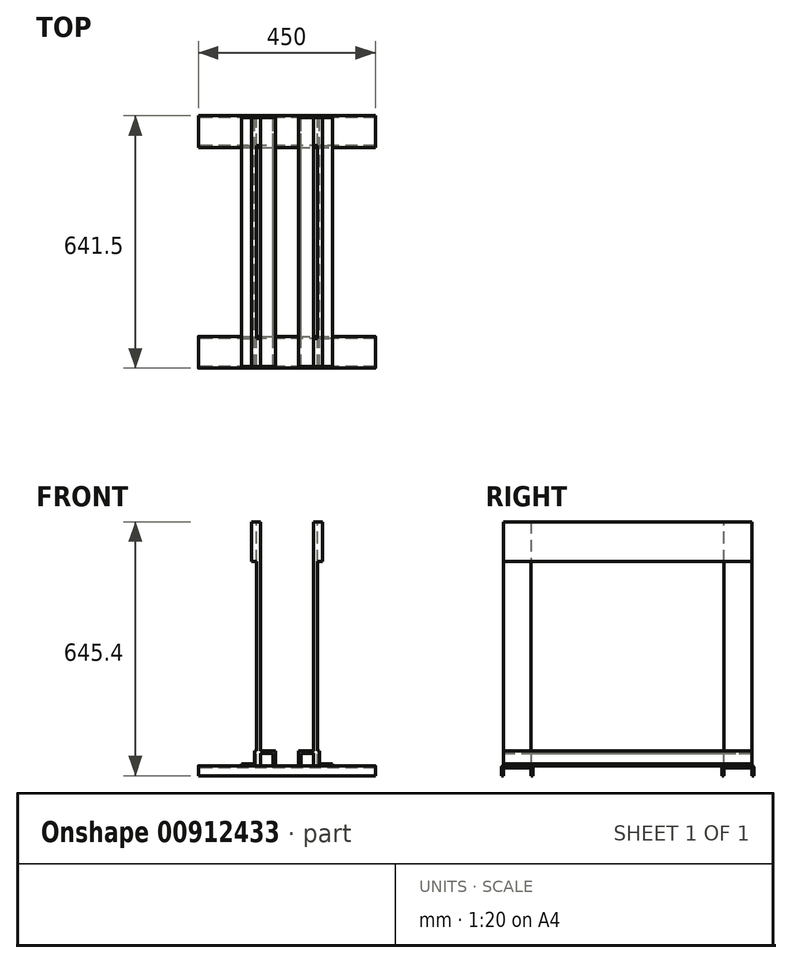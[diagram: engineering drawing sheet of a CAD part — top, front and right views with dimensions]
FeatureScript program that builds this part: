
annotation { "Feature Type Name" : "Feature", "Feature Type Description" : "" }
export const myFeature = defineFeature(function(context is Context, id is Id, definition is map)
    precondition{}
    {
        {
            var Q0;
            Q0=qCreatedBy(makeId("Front.planeOp"),FACE);
            var sketch = newSketch(context, id + "F0", { "sketchPlane" : qUnion([Q0])});
            skLineSegment(sketch, "E0.bottom", {"start": v(0, 0) * mm, "end": v(-10.45, 0) * mm});
            skLineSegment(sketch, "E0.top", {"start": v(0, 620) * mm, "end": v(-10.45, 620) * mm});
            skLineSegment(sketch, "E0.left", {"start": v(0, 0) * mm, "end": v(0, 620) * mm});
            skLineSegment(sketch, "E0.right", {"start": v(-10.45, 0) * mm, "end": v(-10.45, 620) * mm});
            skLineSegment(sketch, "E1", {"start": v(0, 38.1) * mm, "end": v(38.1, 38.1) * mm});
            skLineSegment(sketch, "E2", {"start": v(38.1, 38.1) * mm, "end": v(38.1, 0) * mm});
            skLineSegment(sketch, "E3", {"start": v(38.1, 0) * mm, "end": v(31.75, 0) * mm});
            skLineSegment(sketch, "E4", {"start": v(31.75, 0) * mm, "end": v(31.75, 31.75) * mm});
            skLineSegment(sketch, "E5", {"start": v(31.75, 31.75) * mm, "end": v(0, 31.75) * mm});
            skSolve(sketch);
        }
        {
            var Q0;
            {var subQ0=sQuery(id+"F0.wireOp",EDGE,"E1");Q0=makeQuery(id+"F0.imprint","IMPRINT",FACE,{"disambiguationData":[TD([[makeQuery(id+"F0.imprint","IMPRINT",EDGE,{"derivedFrom":subQ0}),-1.0]])]});}
            extrude(context, id + "F1", {"entities" : qUnion([Q0]), "depth" : 631.5 * mm, "offsetDistance" : 25 * mm});
        }
        {
            var Q0;
            {var subQ3=sQuery(id+"F0.wireOp",EDGE,"E0.bottom");Q0=makeQuery(id+"F0.imprint","IMPRINT",FACE,{"disambiguationData":[TD([[makeQuery(id+"F0.imprint","IMPRINT",EDGE,{"derivedFrom":subQ3}),-1.0]])]});}
            extrude(context, id + "F2", {"entities" : qUnion([Q0]), "operationType" : NewBodyOperationType.ADD, "depth" : 70.75 * mm, "offsetDistance" : 25 * mm});
        }
        {
            var Q0;
            Q0=qCreatedBy(makeId("Top.planeOp"),FACE);
            var sketch = newSketch(context, id + "F3", { "sketchPlane" : qUnion([Q0])});
            skLineSegment(sketch, "E6.bottom", {"start": v(0, -631.5) * mm, "end": v(-10.45, -631.5) * mm});
            skLineSegment(sketch, "E6.top", {"start": v(0, -560.75) * mm, "end": v(-10.45, -560.75) * mm});
            skLineSegment(sketch, "E6.left", {"start": v(0, -631.5) * mm, "end": v(0, -560.75) * mm});
            skLineSegment(sketch, "E6.right", {"start": v(-10.45, -631.5) * mm, "end": v(-10.45, -560.75) * mm});
            skSolve(sketch);
        }
        {
            var Q0;
            Q0 = qSketchRegion(id + "F3", true);
            extrude(context, id + "F4", {"entities" : qUnion([Q0]), "operationType" : NewBodyOperationType.ADD, "depth" : 620 * mm, "offsetDistance" : 25 * mm});
        }
        {
            var Q0;
            Q0=qCreatedBy(makeId("Top.planeOp"),FACE);
            var sketch = newSketch(context, id + "F5", { "sketchPlane" : qUnion([Q0])});
            skLineSegment(sketch, "E7.bottom", {"start": v(-157.8, 5) * mm, "end": v(292.2, 5) * mm});
            skLineSegment(sketch, "E7.top", {"start": v(-157.8, -75.75) * mm, "end": v(292.2, -75.75) * mm});
            skLineSegment(sketch, "E7.left", {"start": v(-157.8, 5) * mm, "end": v(-157.8, -75.75) * mm});
            skLineSegment(sketch, "E7.right", {"start": v(292.2, 5) * mm, "end": v(292.2, -75.75) * mm});
            skLineSegment(sketch, "E8.bottom", {"start": v(-157.8, -636.5) * mm, "end": v(292.2, -636.5) * mm});
            skLineSegment(sketch, "E8.top", {"start": v(-157.8, -555.75) * mm, "end": v(292.2, -555.75) * mm});
            skLineSegment(sketch, "E8.left", {"start": v(-157.8, -636.5) * mm, "end": v(-157.8, -555.75) * mm});
            skLineSegment(sketch, "E8.right", {"start": v(292.2, -636.5) * mm, "end": v(292.2, -555.75) * mm});
            skSolve(sketch);
        }
        {
            var Q0;
            Q0 = qSketchRegion(id + "F5", true);
            extrude(context, id + "F6", {"entities" : qUnion([Q0]), "operationType" : NewBodyOperationType.ADD, "oppositeDirection" : true, "depth" : 25.4 * mm, "offsetDistance" : 25 * mm});
        }
        {
            var Q0;
            Q0=makeQuery(id+"F6.opExtrude","CAP_EDGE",EDGE,{"disambiguationData":[OSD([sQuery(id+"F5.wireOp",EDGE,"E8.bottom")])],"isStart":true});
            var Q1;
            {var subQ0=sQuery(id+"F5.wireOp",EDGE,"E8.top");var subQ1=makeQuery(id+"F6.opExtrude","SWEPT_FACE",FACE,{"disambiguationData":[OSD([subQ0])]});var subQ2=sQuery(id+"F5.wireOp",EDGE,"E8.right");var subQ3=makeQuery(id+"F6.opExtrude","CAP_FACE",FACE,{"disambiguationData":[OSD([sQuery(id+"F5.wireOp",EDGE,"E8.bottom"),subQ0,sQuery(id+"F5.wireOp",EDGE,"E8.left"),subQ2])],"isStart":true});Q1=makeQuery(id+"F6.boolean.opBoolean","SPLIT",EDGE,{"disambiguationData":[topologyDisambiguationEdgeConnected([subQ3,subQ1]),TD([makeQuery(id+"F1.opExtrude","SWEPT_FACE",FACE,{"disambiguationData":[OSD([sQuery(id+"F0.wireOp",EDGE,"E2")])]})])],"derivedFrom":makeQuery(id+"F6.opExtrude","CAP_EDGE",EDGE,{"disambiguationData":[OSD([subQ0])],"isStart":true})});}
            var Q2;
            {var subQ0=sQuery(id+"F5.wireOp",EDGE,"E8.top");var subQ1=makeQuery(id+"F6.opExtrude","SWEPT_FACE",FACE,{"disambiguationData":[OSD([subQ0])]});var subQ2=sQuery(id+"F5.wireOp",EDGE,"E8.left");var subQ3=makeQuery(id+"F6.opExtrude","CAP_FACE",FACE,{"disambiguationData":[OSD([sQuery(id+"F5.wireOp",EDGE,"E8.bottom"),subQ0,subQ2,sQuery(id+"F5.wireOp",EDGE,"E8.right")])],"isStart":true});Q2=makeQuery(id+"F6.boolean.opBoolean","SPLIT",EDGE,{"disambiguationData":[topologyDisambiguationEdgeConnected([subQ3,subQ1]),TD([makeQuery(id+"F1.opExtrude","SWEPT_FACE",FACE,{"disambiguationData":[OSD([sQuery(id+"F0.wireOp",EDGE,"E4")])]})])],"derivedFrom":makeQuery(id+"F6.opExtrude","CAP_EDGE",EDGE,{"disambiguationData":[OSD([subQ0])],"isStart":true})});}
            var Q3;
            {var subQ0=sQuery(id+"F5.wireOp",EDGE,"E7.top");var subQ1=makeQuery(id+"F6.opExtrude","SWEPT_FACE",FACE,{"disambiguationData":[OSD([subQ0])]});var subQ2=sQuery(id+"F5.wireOp",EDGE,"E7.right");var subQ3=makeQuery(id+"F6.opExtrude","CAP_FACE",FACE,{"disambiguationData":[OSD([sQuery(id+"F5.wireOp",EDGE,"E7.bottom"),subQ0,sQuery(id+"F5.wireOp",EDGE,"E7.left"),subQ2])],"isStart":true});Q3=makeQuery(id+"F6.boolean.opBoolean","SPLIT",EDGE,{"disambiguationData":[topologyDisambiguationEdgeConnected([subQ3,subQ1]),TD([makeQuery(id+"F1.opExtrude","SWEPT_FACE",FACE,{"disambiguationData":[OSD([sQuery(id+"F0.wireOp",EDGE,"E2")])]})])],"derivedFrom":makeQuery(id+"F6.opExtrude","CAP_EDGE",EDGE,{"disambiguationData":[OSD([subQ0])],"isStart":true})});}
            var Q4;
            {var subQ0=sQuery(id+"F5.wireOp",EDGE,"E7.top");var subQ1=makeQuery(id+"F6.opExtrude","SWEPT_FACE",FACE,{"disambiguationData":[OSD([subQ0])]});var subQ2=sQuery(id+"F5.wireOp",EDGE,"E7.left");var subQ3=makeQuery(id+"F6.opExtrude","CAP_FACE",FACE,{"disambiguationData":[OSD([sQuery(id+"F5.wireOp",EDGE,"E7.bottom"),subQ0,subQ2,sQuery(id+"F5.wireOp",EDGE,"E7.right")])],"isStart":true});Q4=makeQuery(id+"F6.boolean.opBoolean","SPLIT",EDGE,{"disambiguationData":[topologyDisambiguationEdgeConnected([subQ3,subQ1]),TD([makeQuery(id+"F1.opExtrude","SWEPT_FACE",FACE,{"disambiguationData":[OSD([sQuery(id+"F0.wireOp",EDGE,"E4")])]})])],"derivedFrom":makeQuery(id+"F6.opExtrude","CAP_EDGE",EDGE,{"disambiguationData":[OSD([subQ0])],"isStart":true})});}
            var Q5;
            Q5=makeQuery(id+"F6.opExtrude","CAP_EDGE",EDGE,{"disambiguationData":[OSD([sQuery(id+"F5.wireOp",EDGE,"E7.bottom")])],"isStart":true});
            fillet(context, id + "F7", {"entities" : qUnion([Q0, Q1, Q2, Q3, Q4, Q5]), "radius" : 5 * mm, "tangentPropagation" : true, "allowEdgeOverflow" : false});
        }
        {
            var Q0;
            Q0=qCreatedBy(makeId("Front.planeOp"),FACE);
            var sketch = newSketch(context, id + "F8", { "sketchPlane" : qUnion([Q0])});
            skLineSegment(sketch, "E9.bottom", {"start": v(134.4, 0) * mm, "end": v(144.85, 0) * mm});
            skLineSegment(sketch, "E9.top", {"start": v(134.4, 620) * mm, "end": v(144.85, 620) * mm});
            skLineSegment(sketch, "E9.left", {"start": v(134.4, 0) * mm, "end": v(134.4, 620) * mm});
            skLineSegment(sketch, "E9.right", {"start": v(144.85, 0) * mm, "end": v(144.85, 620) * mm});
            skLineSegment(sketch, "E10", {"start": v(134.4, 38.1) * mm, "end": v(96.3, 38.1) * mm});
            skLineSegment(sketch, "E11", {"start": v(96.3, 38.1) * mm, "end": v(96.3, 0) * mm});
            skLineSegment(sketch, "E12", {"start": v(96.3, 0) * mm, "end": v(102.65, 0) * mm});
            skLineSegment(sketch, "E13", {"start": v(102.65, 0) * mm, "end": v(102.65, 31.75) * mm});
            skLineSegment(sketch, "E14", {"start": v(102.65, 31.75) * mm, "end": v(134.4, 31.75) * mm});
            skSolve(sketch);
        }
        {
            var Q0;
            {var subQ0=sQuery(id+"F8.wireOp",EDGE,"E10");Q0=makeQuery(id+"F8.imprint","IMPRINT",FACE,{"disambiguationData":[TD([[makeQuery(id+"F8.imprint","IMPRINT",EDGE,{"derivedFrom":subQ0}),1.0]])]});}
            extrude(context, id + "F9", {"entities" : qUnion([Q0]), "operationType" : NewBodyOperationType.ADD, "depth" : 631.5 * mm, "offsetDistance" : 25 * mm});
        }
        {
            var Q0;
            Q0 = qSketchRegion(id + "F8", true);
            extrude(context, id + "F10", {"entities" : qUnion([Q0]), "operationType" : NewBodyOperationType.ADD, "depth" : 70.75 * mm, "offsetDistance" : 25 * mm});
        }
        {
            var Q0;
            Q0=qCreatedBy(makeId("Top.planeOp"),FACE);
            var sketch = newSketch(context, id + "F11", { "sketchPlane" : qUnion([Q0])});
            skLineSegment(sketch, "E15.bottom", {"start": v(134.4, -631.5) * mm, "end": v(144.85, -631.5) * mm});
            skLineSegment(sketch, "E15.top", {"start": v(134.4, -560.75) * mm, "end": v(144.85, -560.75) * mm});
            skLineSegment(sketch, "E15.left", {"start": v(134.4, -631.5) * mm, "end": v(134.4, -560.75) * mm});
            skLineSegment(sketch, "E15.right", {"start": v(144.85, -631.5) * mm, "end": v(144.85, -560.75) * mm});
            skSolve(sketch);
        }
        {
            var Q0;
            Q0 = qSketchRegion(id + "F11", true);
            extrude(context, id + "F12", {"entities" : qUnion([Q0]), "operationType" : NewBodyOperationType.ADD, "depth" : 620 * mm, "offsetDistance" : 25 * mm});
        }
        {
            var Q0;
            Q0=qCreatedBy(makeId("Front.planeOp"),FACE);
            var sketch = newSketch(context, id + "F13", { "sketchPlane" : qUnion([Q0])});
            skLineSegment(sketch, "E16.bottom", {"start": v(-10.45, 620) * mm, "end": v(-23.2, 620) * mm});
            skLineSegment(sketch, "E16.top", {"start": v(-10.45, 518.8) * mm, "end": v(-23.2, 518.8) * mm});
            skLineSegment(sketch, "E16.left", {"start": v(-10.45, 620) * mm, "end": v(-10.45, 518.8) * mm});
            skLineSegment(sketch, "E16.right", {"start": v(-23.2, 620) * mm, "end": v(-23.2, 518.8) * mm});
            skLineSegment(sketch, "E17.1.0.0", {"start": v(157.6, 620) * mm, "end": v(144.85, 620) * mm});
            skLineSegment(sketch, "E17.1.0.1", {"start": v(144.85, 620) * mm, "end": v(144.85, 518.8) * mm});
            skLineSegment(sketch, "E17.1.0.2", {"start": v(157.6, 518.8) * mm, "end": v(144.85, 518.8) * mm});
            skLineSegment(sketch, "E17.1.0.3", {"start": v(157.6, 620) * mm, "end": v(157.6, 518.8) * mm});
            skLineSegment(sketch, "E17.direction1", {"start": v(-23.2, 620) * mm, "end": v(144.85, 620) * mm, "construction": true});
            skSolve(sketch);
        }
        {
            var Q0;
            Q0 = qSketchRegion(id + "F13", true);
            extrude(context, id + "F14", {"entities" : qUnion([Q0]), "operationType" : NewBodyOperationType.ADD, "depth" : 631.5 * mm, "offsetDistance" : 25 * mm});
        }
        {
            var Q0;
            Q0=qCreatedBy(makeId("Front.planeOp"),FACE);
            var sketch = newSketch(context, id + "F15", { "sketchPlane" : qUnion([Q0])});
            skLineSegment(sketch, "E18", {"start": v(-48.55, 0) * mm, "end": v(-10.45, 0) * mm});
            skLineSegment(sketch, "E19", {"start": v(-10.45, 0) * mm, "end": v(-10.45, 38.1) * mm});
            skLineSegment(sketch, "E20", {"start": v(-10.45, 38.1) * mm, "end": v(-15.21, 38.1) * mm});
            skLineSegment(sketch, "E21", {"start": v(-15.21, 38.1) * mm, "end": v(-15.21, 4.76) * mm});
            skLineSegment(sketch, "E22", {"start": v(-15.21, 4.76) * mm, "end": v(-48.55, 4.76) * mm});
            skLineSegment(sketch, "E23", {"start": v(-48.55, 4.76) * mm, "end": v(-48.55, 0) * mm});
            skLineSegment(sketch, "E24", {"start": v(182.95, 0) * mm, "end": v(144.85, 0) * mm});
            skLineSegment(sketch, "E25", {"start": v(144.85, 0) * mm, "end": v(144.85, 38.1) * mm});
            skLineSegment(sketch, "E26", {"start": v(144.85, 38.1) * mm, "end": v(149.61, 38.1) * mm});
            skLineSegment(sketch, "E27", {"start": v(149.61, 38.1) * mm, "end": v(149.61, 4.76) * mm});
            skLineSegment(sketch, "E28", {"start": v(149.61, 4.76) * mm, "end": v(182.95, 4.76) * mm});
            skLineSegment(sketch, "E29", {"start": v(182.95, 4.76) * mm, "end": v(182.95, 0) * mm});
            skSolve(sketch);
        }
        {
            var Q0;
            Q0 = qSketchRegion(id + "F15", true);
            extrude(context, id + "F16", {"entities" : qUnion([Q0]), "operationType" : NewBodyOperationType.ADD, "depth" : 631.5 * mm, "offsetDistance" : 25 * mm});
        }
        {
            var Q0;
            Q0=qCreatedBy(makeId("Right.planeOp"),FACE);
            var sketch = newSketch(context, id + "F17", { "sketchPlane" : qUnion([Q0])});
            skLineSegment(sketch, "E30.bottom", {"start": v(-631.5, -25.4) * mm, "end": v(-560.75, -25.4) * mm});
            skLineSegment(sketch, "E30.top", {"start": v(-626.5, -5) * mm, "end": v(-565.75, -5) * mm});
            skLineSegment(sketch, "E30.left", {"start": v(-631.5, -25.4) * mm, "end": v(-631.5, -10) * mm});
            skLineSegment(sketch, "E30.right", {"start": v(-560.75, -25.4) * mm, "end": v(-560.75, -10) * mm});
            skPoint(sketch, "E31.visualSharp", {"position": v(-631.5, -5) * mm});
            skArc(sketch, "E31.filletArc", {"start": v(-626.5, -5) * mm, "mid": v(-630.04, -6.46) * mm, "end": v(-631.5, -10) * mm});
            skPoint(sketch, "E32.visualSharp", {"position": v(-560.75, -5) * mm});
            skArc(sketch, "E32.filletArc", {"start": v(-560.75, -10) * mm, "mid": v(-562.21, -6.46) * mm, "end": v(-565.75, -5) * mm});
            skArc(sketch, "E33.1.0.0", {"start": v(-65.75, -5) * mm, "mid": v(-69.29, -6.46) * mm, "end": v(-70.75, -10) * mm});
            skLineSegment(sketch, "E33.1.0.1", {"start": v(-70.75, -25.4) * mm, "end": v(-70.75, -10) * mm});
            skLineSegment(sketch, "E33.1.0.2", {"start": v(-70.75, -25.4) * mm, "end": v(0, -25.4) * mm});
            skLineSegment(sketch, "E33.1.0.3", {"start": v(0, -25.4) * mm, "end": v(0, -10) * mm});
            skArc(sketch, "E33.1.0.4", {"start": v(0, -10) * mm, "mid": v(-1.46, -6.46) * mm, "end": v(-5, -5) * mm});
            skLineSegment(sketch, "E33.1.0.5", {"start": v(-65.75, -5) * mm, "end": v(-5, -5) * mm});
            skLineSegment(sketch, "E33.direction1", {"start": v(-631.5, -10) * mm, "end": v(-70.75, -10) * mm, "construction": true});
            skSolve(sketch);
        }
        {
            var Q0;
            Q0 = qSketchRegion(id + "F17", true);
            extrude(context, id + "F18", {"entities" : qUnion([Q0]), "operationType" : NewBodyOperationType.REMOVE, "depth" : 300 * mm, "offsetDistance" : 25 * mm});
        }
        {
            var Q0;
            Q0 = qSketchRegion(id + "F17", true);
            extrude(context, id + "F19", {"entities" : qUnion([Q0]), "operationType" : NewBodyOperationType.REMOVE, "oppositeDirection" : true, "depth" : 300 * mm, "offsetDistance" : 25 * mm});
        }
    });
